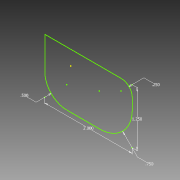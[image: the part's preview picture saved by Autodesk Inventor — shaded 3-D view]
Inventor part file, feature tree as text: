
AUTODESK INVENTOR PART (.ipt)
format: ipt  version: 2015 (Build 190159000, 159)  size: 65,024 bytes
history: native  units: in
note: dims shown in document units (in); Inventor stores cm internally (conversion verified against a paired STEP export)
features: sketch x1
ambient origin geometry x8: Origin, YZ Plane, XZ Plane, XY Plane, X Axis, Y Axis, Z Axis, Center Point
feature tree (1):
  sketch  "Sketch1"  dims[d0=2.0in d1=1.25in d2=0.5in d3=0.75in d4=0.25in]
